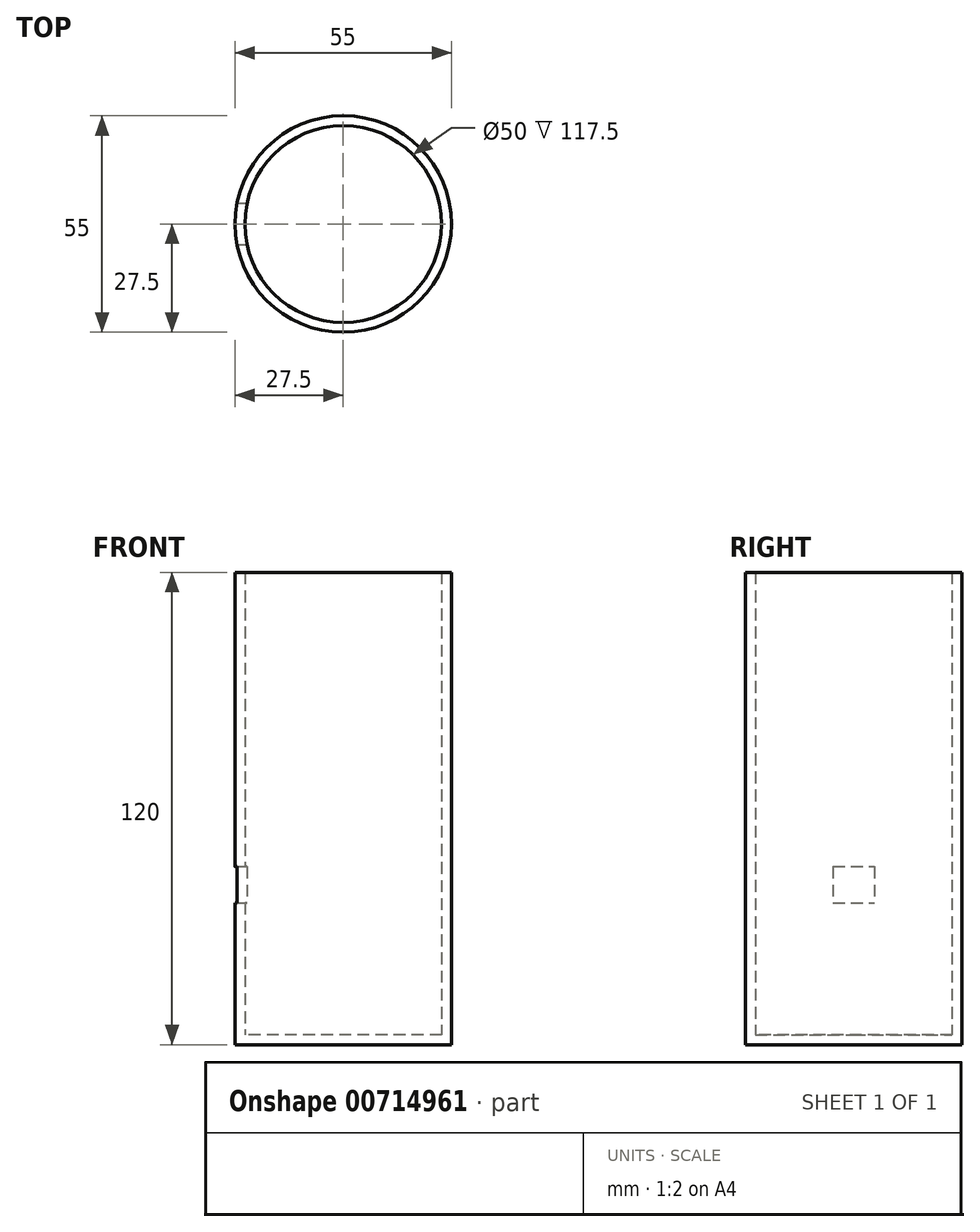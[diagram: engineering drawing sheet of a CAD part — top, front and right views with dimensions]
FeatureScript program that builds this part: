
annotation { "Feature Type Name" : "Feature", "Feature Type Description" : "" }
export const myFeature = defineFeature(function(context is Context, id is Id, definition is map)
    precondition{}
    {
        {
            var Q0;
            Q0=qCreatedBy(makeId("Top.planeOp"),FACE);
            var sketch = newSketch(context, id + "F0", { "sketchPlane" : qUnion([Q0])});
            skCircle(sketch, "E0", {"center": v(0, 0) * mm, "radius": 27.5 * mm});
            skSolve(sketch);
        }
        {
            var Q0;
            Q0=makeQuery(id+"F0.imprint","IMPRINT",FACE,{"disambiguationData":[TD([[makeQuery(id+"F0.imprint","IMPRINT",EDGE,{"derivedFrom":sQuery(id+"F0.wireOp",EDGE,"E0")}),1.0]])]});
            extrude(context, id + "F1", {"entities" : qUnion([Q0]), "depth" : 120 * mm, "offsetDistance" : 25 * mm});
        }
        {
            var Q0;
            Q0=makeQuery(id+"F1.opExtrude","CAP_FACE",FACE,{"disambiguationData":[OSD([sQuery(id+"F0.wireOp",EDGE,"E0")])],"isStart":false});
            shell(context, id + "F2", {"entities" : qUnion([Q0]), "thickness" : 2.5 * mm});
        }
        {
            var Q0;
            Q0=qCreatedBy(makeId("Right.planeOp"),FACE);
            var sketch = newSketch(context, id + "F3", { "sketchPlane" : qUnion([Q0])});
            skLineSegment(sketch, "E1.bottom", {"start": v(-5.28, 36.06) * mm, "end": v(5.28, 36.06) * mm});
            skLineSegment(sketch, "E1.top", {"start": v(-5.28, 45.25) * mm, "end": v(5.28, 45.25) * mm});
            skLineSegment(sketch, "E1.left", {"start": v(-5.28, 36.06) * mm, "end": v(-5.28, 45.25) * mm});
            skLineSegment(sketch, "E1.right", {"start": v(5.28, 36.06) * mm, "end": v(5.28, 45.25) * mm});
            skSolve(sketch);
        }
        {
            var Q0;
            Q0 = qSketchRegion(id + "F3", true);
            extrude(context, id + "F4", {"entities" : qUnion([Q0]), "operationType" : NewBodyOperationType.REMOVE, "endBound" : BoundingType.THROUGH_ALL, "oppositeDirection" : true, "depth" : 25 * mm, "offsetDistance" : 25 * mm});
        }
    });
